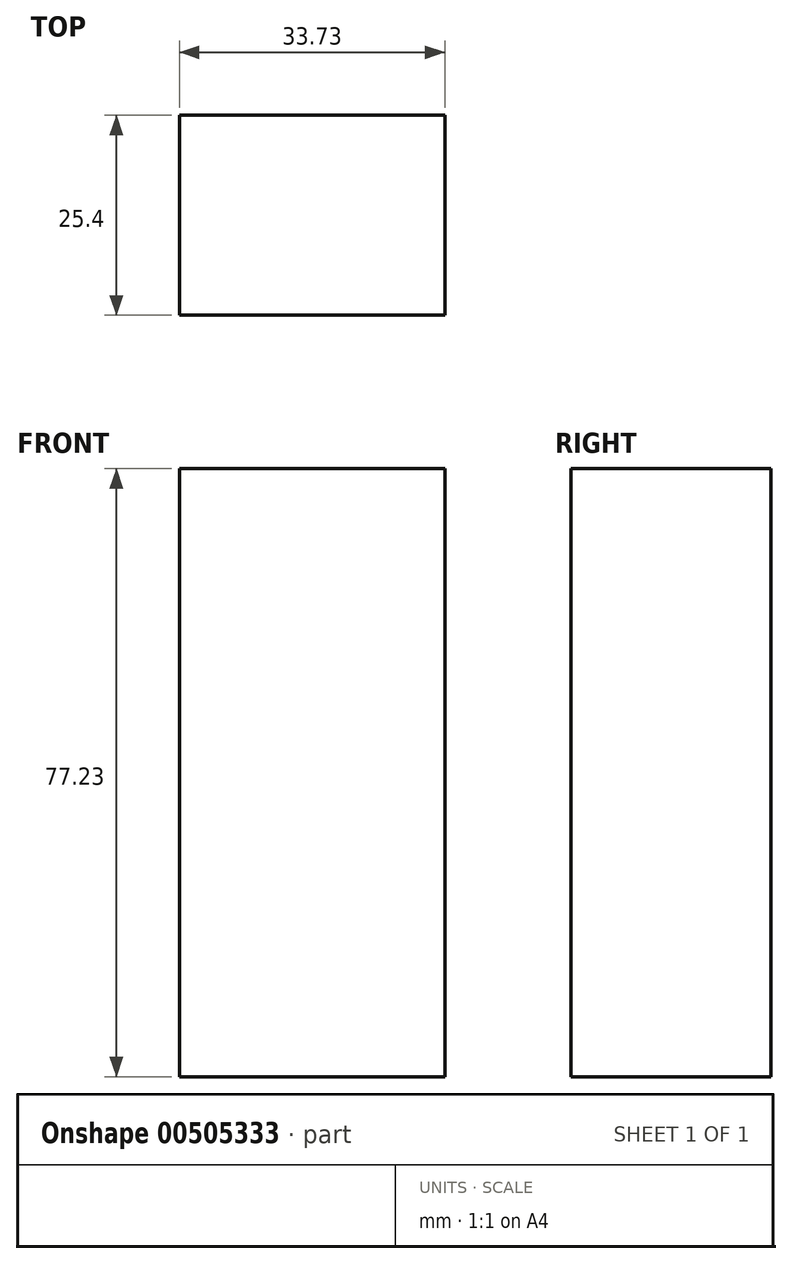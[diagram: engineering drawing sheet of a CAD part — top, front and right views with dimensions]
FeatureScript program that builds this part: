
annotation { "Feature Type Name" : "Feature", "Feature Type Description" : "" }
export const myFeature = defineFeature(function(context is Context, id is Id, definition is map)
    precondition{}
    {
        {
            var Q0;
            Q0=qCreatedBy(makeId("Front.planeOp"),FACE);
            var sketch = newSketch(context, id + "F0", { "sketchPlane" : qUnion([Q0])});
            skLineSegment(sketch, "E0.bottom", {"start": v(-17.1, 24.44) * mm, "end": v(16.62, 24.44) * mm});
            skLineSegment(sketch, "E0.top", {"start": v(-17.1, -52.8) * mm, "end": v(16.62, -52.8) * mm});
            skLineSegment(sketch, "E0.left", {"start": v(-17.1, 24.44) * mm, "end": v(-17.1, -52.8) * mm});
            skLineSegment(sketch, "E0.right", {"start": v(16.62, 24.44) * mm, "end": v(16.62, -52.8) * mm});
            skSolve(sketch);
        }
        {
            var Q0;
            Q0 = qSketchRegion(id + "F0", true);
            extrude(context, id + "F1", {"entities" : qUnion([Q0]), "depth" : 25.4 * mm});
        }
    });
